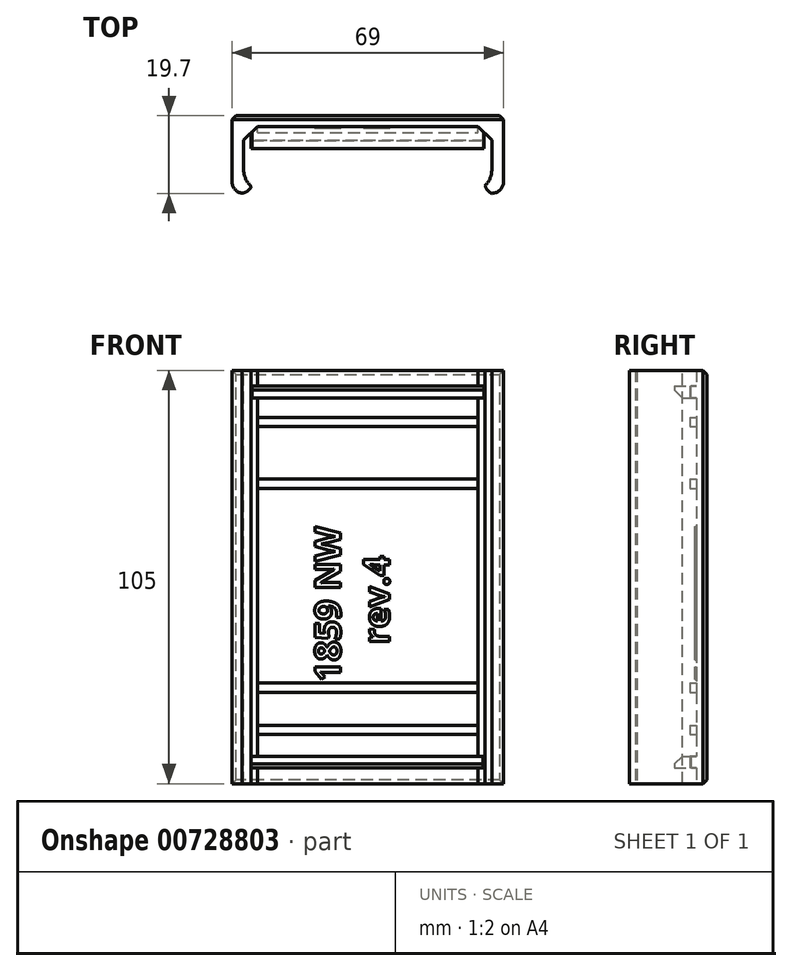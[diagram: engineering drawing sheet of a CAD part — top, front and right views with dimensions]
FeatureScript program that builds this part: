
annotation { "Feature Type Name" : "Feature", "Feature Type Description" : "" }
export const myFeature = defineFeature(function(context is Context, id is Id, definition is map)
    precondition{}
    {
        {
            var Q0;
            Q0=qCreatedBy(makeId("Top.planeOp"),FACE);
            var sketch = newSketch(context, id + "F0", { "sketchPlane" : qUnion([Q0])});
            skLineSegment(sketch, "E0", {"start": v(51.67, 0) * mm, "end": v(-17.33, 0) * mm});
            skLineSegment(sketch, "E1", {"start": v(-17.33, 0) * mm, "end": v(-17.33, -16.7) * mm});
            skLineSegment(sketch, "E2", {"start": v(-14.33, -19.7) * mm, "end": v(-12.53, -19.7) * mm});
            skLineSegment(sketch, "E3", {"start": v(-12.53, -19.7) * mm, "end": v(-12.53, -18.2) * mm});
            skLineSegment(sketch, "E4", {"start": v(-13.53, -17.2) * mm, "end": v(-14.33, -17.2) * mm});
            skLineSegment(sketch, "E5", {"start": v(-14.33, -17.2) * mm, "end": v(-14.33, -2.7) * mm});
            skLineSegment(sketch, "E6", {"start": v(-14.33, -2.7) * mm, "end": v(48.67, -2.7) * mm});
            skLineSegment(sketch, "E7", {"start": v(48.67, -2.7) * mm, "end": v(48.67, -17.2) * mm});
            skLineSegment(sketch, "E8", {"start": v(48.67, -17.2) * mm, "end": v(47.87, -17.2) * mm});
            skLineSegment(sketch, "E9", {"start": v(46.87, -18.2) * mm, "end": v(46.87, -19.7) * mm});
            skLineSegment(sketch, "E10", {"start": v(46.87, -19.7) * mm, "end": v(48.67, -19.7) * mm});
            skLineSegment(sketch, "E11", {"start": v(51.67, -16.7) * mm, "end": v(51.67, 0) * mm});
            skPoint(sketch, "E12.visualSharp", {"position": v(-17.33, 0) * mm});
            skLineSegment(sketch, "E12.filletArc", {"start": v(-17.33, 0) * mm, "end": v(-17.33, 0) * mm});
            skPoint(sketch, "E13.visualSharp", {"position": v(51.67, 0) * mm});
            skLineSegment(sketch, "E13.filletArc", {"start": v(51.67, 0) * mm, "end": v(51.67, 0) * mm});
            skLineSegment(sketch, "E14.filletArc", {"start": v(-14.33, -2.7) * mm, "end": v(-14.33, -2.7) * mm});
            skPoint(sketch, "E15.visualSharp", {"position": v(48.67, -2.7) * mm});
            skLineSegment(sketch, "E15.filletArc", {"start": v(48.67, -2.7) * mm, "end": v(48.67, -2.7) * mm});
            skPoint(sketch, "E16.visualSharp", {"position": v(-12.53, -17.2) * mm});
            skArc(sketch, "E16.filletArc", {"start": v(-12.53, -18.2) * mm, "mid": v(-12.82, -17.5) * mm, "end": v(-13.53, -17.2) * mm});
            skPoint(sketch, "E17.visualSharp", {"position": v(46.87, -17.2) * mm});
            skArc(sketch, "E17.filletArc", {"start": v(47.87, -17.2) * mm, "mid": v(47.17, -17.5) * mm, "end": v(46.87, -18.2) * mm});
            skPoint(sketch, "E18.visualSharp", {"position": v(51.67, -19.7) * mm});
            skArc(sketch, "E18.filletArc", {"start": v(48.67, -19.7) * mm, "mid": v(50.8, -18.82) * mm, "end": v(51.67, -16.7) * mm});
            skPoint(sketch, "E19.visualSharp", {"position": v(-17.33, -19.7) * mm});
            skArc(sketch, "E19.filletArc", {"start": v(-17.33, -16.7) * mm, "mid": v(-16.45, -18.82) * mm, "end": v(-14.33, -19.7) * mm});
            skLineSegment(sketch, "E20", {"start": v(17.17, 21.1) * mm, "end": v(17.17, -24.08) * mm, "construction": true});
            skPoint(sketch, "E20.startSnap0", {"position": v(17.17, 0) * mm});
            skSolve(sketch);
        }
        {
            var Q0;
            Q0=makeQuery(id+"F0.imprint","IMPRINT",FACE,{"disambiguationData":[TD([[makeQuery(id+"F0.imprint","IMPRINT",EDGE,{"derivedFrom":sQuery(id+"F0.wireOp",EDGE,"E0")}),1.0]])]});
            extrude(context, id + "F1", {"entities" : qUnion([Q0]), "depth" : 105 * mm, "offsetDistance" : 25 * mm});
        }
        {
            var Q0;
            Q0=makeQuery(id+"F1.opExtrude","SWEPT_EDGE",EDGE,{"disambiguationData":[OSD([sQuery(id+"F0.wireOp",EDGE,"E9"),sQuery(id+"F0.wireOp",EDGE,"E10")])]});
            var Q1;
            Q1=makeQuery(id+"F1.opExtrude","SWEPT_EDGE",EDGE,{"disambiguationData":[OSD([sQuery(id+"F0.wireOp",EDGE,"E2"),sQuery(id+"F0.wireOp",EDGE,"E3")])]});
            fillet(context, id + "F2", {"entities" : qUnion([Q0, Q1]), "radius" : 3 * mm, "tangentPropagation" : true, "allowEdgeOverflow" : false});
        }
        {
            var Q0;
            Q0=makeQuery(id+"F1.opExtrude","SWEPT_EDGE",EDGE,{"disambiguationData":[OSD([sQuery(id+"F0.wireOp",EDGE,"E7"),sQuery(id+"F0.wireOp",EDGE,"E8")])]});
            var Q1;
            Q1=makeQuery(id+"F1.opExtrude","SWEPT_EDGE",EDGE,{"disambiguationData":[OSD([sQuery(id+"F0.wireOp",EDGE,"E4"),sQuery(id+"F0.wireOp",EDGE,"E5")])]});
            fillet(context, id + "F3", {"entities" : qUnion([Q0, Q1]), "radius" : 5 * mm, "tangentPropagation" : true, "allowEdgeOverflow" : false});
        }
        {
            var Q0;
            Q0=makeQuery(id+"F1.opExtrude","SWEPT_FACE",FACE,{"disambiguationData":[OSD([sQuery(id+"F0.wireOp",EDGE,"E6")])]});
            var sketch = newSketch(context, id + "F4", { "sketchPlane" : qUnion([Q0])});
            skPoint(sketch, "E21", {"position": v(17.17, 52.5) * mm});
            skPoint(sketch, "E21.positionSnap0", {"position": v(48.67, 52.5) * mm});
            skPoint(sketch, "E21.positionSnap1", {"position": v(17.17, 105) * mm});
            skLineSegment(sketch, "E22.bottom", {"start": v(-9.33, 91) * mm, "end": v(43.67, 91) * mm});
            skLineSegment(sketch, "E22.top", {"start": v(-9.33, 14) * mm, "end": v(43.67, 14) * mm});
            skLineSegment(sketch, "E22.left", {"start": v(-9.33, 91) * mm, "end": v(-9.33, 14) * mm});
            skLineSegment(sketch, "E22.right", {"start": v(43.67, 91) * mm, "end": v(43.67, 14) * mm});
            skLineSegment(sketch, "E23.0", {"start": v(-6.33, 88) * mm, "end": v(40.67, 88) * mm});
            skLineSegment(sketch, "E23.1", {"start": v(-6.33, 88) * mm, "end": v(-6.33, 17) * mm});
            skLineSegment(sketch, "E23.2", {"start": v(-6.33, 17) * mm, "end": v(40.67, 17) * mm});
            skLineSegment(sketch, "E23.3", {"start": v(40.67, 88) * mm, "end": v(40.67, 17) * mm});
            skSolve(sketch);
        }
        {
            var Q0;
            Q0=makeQuery(id+"F2eu8U94Az3jvPq_1.boolean.opBoolean","SPLIT",FACE,{"disambiguationData":[TD([makeQuery(id+"F2eu8U94Az3jvPq_1.opExtrude","SWEPT_FACE",FACE,{"disambiguationData":[OSD([sQuery(id+"F4.wireOp",EDGE,"E23.0")])]})])],"derivedFrom":makeQuery(id+"F1.opExtrude","SWEPT_FACE",FACE,{"disambiguationData":[OSD([sQuery(id+"F0.wireOp",EDGE,"E6")])]})});
            var sketch = newSketch(context, id + "F5", { "sketchPlane" : qUnion([Q0])});
            skText(sketch, "E24", { "text": "1859 NW\n    rev.4", "fontName": "OpenSans-Bold.ttf"});
            const initialGuessF5  = {"E24": [0.01026, 0.02593, 0, 1, 0.00656]};
            skSetInitialGuess(sketch, initialGuessF5);
            skSolve(sketch);
        }
        {
            var Q0;
            Q0 = qSketchRegion(id + "F5", true);
            extrude(context, id + "F6", {"entities" : qUnion([Q0]), "operationType" : NewBodyOperationType.ADD, "depth" : .4 * mm, "offsetDistance" : 25 * mm});
        }
        {
            var Q0;
            Q0=makeQuery(id+"F1.opExtrude","SWEPT_EDGE",EDGE,{"disambiguationData":[OSD([sQuery(id+"F0.wireOp",EDGE,"E5"),sQuery(id+"F0.wireOp",EDGE,"E6")])]});
            var Q1;
            Q1=makeQuery(id+"F1.opExtrude","SWEPT_EDGE",EDGE,{"disambiguationData":[OSD([sQuery(id+"F0.wireOp",EDGE,"E6"),sQuery(id+"F0.wireOp",EDGE,"E7")])]});
            chamfer(context, id + "F7", {"entities" : qUnion([Q0, Q1]), "width" : 3.5 * mm, "tangentPropagation" : true});
        }
        {
            var Q0;
            Q0=makeQuery(id+"F1.opExtrude","SWEPT_EDGE",EDGE,{"disambiguationData":[OSD([sQuery(id+"F0.wireOp",EDGE,"E0"),sQuery(id+"F0.wireOp",EDGE,"E1")])]});
            var Q1;
            Q1=makeQuery(id+"F1.opExtrude","SWEPT_EDGE",EDGE,{"disambiguationData":[OSD([sQuery(id+"F0.wireOp",EDGE,"E0"),sQuery(id+"F0.wireOp",EDGE,"E11")])]});
            var Q2;
            Q2=makeQuery(id+"F1.opExtrude","CAP_EDGE",EDGE,{"disambiguationData":[OSD([sQuery(id+"F0.wireOp",EDGE,"E0")])],"isStart":false});
            var Q3;
            Q3=makeQuery(id+"F1.opExtrude","CAP_EDGE",EDGE,{"disambiguationData":[OSD([sQuery(id+"F0.wireOp",EDGE,"E0")])],"isStart":true});
            chamfer(context, id + "F8", {"entities" : qUnion([Q0, Q1, Q2, Q3]), "width" : 1 * mm, "tangentPropagation" : true});
        }
        {
            var Q0;
            {var subQ9=sQuery(id+"F0.wireOp",EDGE,"E6");var subQ10=sQuery(id+"F0.wireOp",EDGE,"E5");Q0=makeQuery(id+"F6.boolean.opBoolean","SPLIT",FACE,{"disambiguationData":[TD([makeQuery(id+"F1.opExtrude","SWEPT_FACE",FACE,{"disambiguationData":[OSD([subQ10])]})])],"derivedFrom":makeQuery(id+"F1.opExtrude","SWEPT_FACE",FACE,{"disambiguationData":[OSD([subQ9])]})});}
            var sketch = newSketch(context, id + "F9", { "sketchPlane" : qUnion([Q0])});
            skLineSegment(sketch, "E25.bottom", {"start": v(-10.83, 93.1) * mm, "end": v(45.17, 93.1) * mm});
            skLineSegment(sketch, "E25.top", {"start": v(-10.83, 90.75) * mm, "end": v(45.17, 90.75) * mm});
            skLineSegment(sketch, "E25.left", {"start": v(-10.83, 93.1) * mm, "end": v(-10.83, 90.75) * mm});
            skLineSegment(sketch, "E25.right", {"start": v(45.17, 93.1) * mm, "end": v(45.17, 90.75) * mm});
            skLineSegment(sketch, "E26.bottom", {"start": v(-10.83, 77.4) * mm, "end": v(45.17, 77.4) * mm});
            skLineSegment(sketch, "E26.top", {"start": v(-10.83, 75.05) * mm, "end": v(45.17, 75.05) * mm});
            skLineSegment(sketch, "E26.left", {"start": v(-10.83, 77.4) * mm, "end": v(-10.83, 75.05) * mm});
            skLineSegment(sketch, "E26.right", {"start": v(45.17, 77.4) * mm, "end": v(45.17, 75.05) * mm});
            skLineSegment(sketch, "E27.bottom", {"start": v(-10.83, 25.58) * mm, "end": v(45.17, 25.58) * mm});
            skLineSegment(sketch, "E27.top", {"start": v(-10.83, 23.23) * mm, "end": v(45.17, 23.23) * mm});
            skLineSegment(sketch, "E27.left", {"start": v(-10.83, 25.58) * mm, "end": v(-10.83, 23.23) * mm});
            skLineSegment(sketch, "E27.right", {"start": v(45.17, 25.58) * mm, "end": v(45.17, 23.23) * mm});
            skLineSegment(sketch, "E28.bottom", {"start": v(-10.83, 14.86) * mm, "end": v(45.17, 14.86) * mm});
            skLineSegment(sketch, "E28.top", {"start": v(-10.83, 12.52) * mm, "end": v(45.17, 12.52) * mm});
            skLineSegment(sketch, "E28.left", {"start": v(-10.83, 14.86) * mm, "end": v(-10.83, 12.52) * mm});
            skLineSegment(sketch, "E28.right", {"start": v(45.17, 14.86) * mm, "end": v(45.17, 12.52) * mm});
            skLineSegment(sketch, "E29.bottom", {"start": v(-12.26, 101) * mm, "end": v(46.74, 101) * mm});
            skLineSegment(sketch, "E29.top", {"start": v(-12.26, 98) * mm, "end": v(46.74, 98) * mm});
            skLineSegment(sketch, "E29.left", {"start": v(-12.26, 101) * mm, "end": v(-12.26, 98) * mm});
            skLineSegment(sketch, "E29.right", {"start": v(46.74, 101) * mm, "end": v(46.74, 98) * mm});
            skLineSegment(sketch, "E30.bottom", {"start": v(-12.5, 7) * mm, "end": v(46.5, 7) * mm});
            skLineSegment(sketch, "E30.top", {"start": v(-12.5, 4) * mm, "end": v(46.5, 4) * mm});
            skLineSegment(sketch, "E30.left", {"start": v(-12.5, 7) * mm, "end": v(-12.5, 4) * mm});
            skLineSegment(sketch, "E30.right", {"start": v(46.5, 7) * mm, "end": v(46.5, 4) * mm});
            skSolve(sketch);
        }
        {
            var Q0;
            Q0 = qSketchRegion(id + "F9", true);
            extrude(context, id + "F10", {"entities" : qUnion([Q0]), "operationType" : NewBodyOperationType.ADD, "depth" : 1.6 * mm, "offsetDistance" : 25 * mm});
        }
        {
            var Q0;
            Q0=makeQuery(id+"F10.opExtrude","CAP_FACE",FACE,{"disambiguationData":[OSD([sQuery(id+"F9.wireOp",EDGE,"E30.bottom"),sQuery(id+"F9.wireOp",EDGE,"E30.top"),sQuery(id+"F9.wireOp",EDGE,"E30.left"),sQuery(id+"F9.wireOp",EDGE,"E30.right")])],"isStart":false});
            var Q1;
            Q1=makeQuery(id+"F10.opExtrude","CAP_FACE",FACE,{"disambiguationData":[OSD([sQuery(id+"F9.wireOp",EDGE,"E29.bottom"),sQuery(id+"F9.wireOp",EDGE,"E29.top"),sQuery(id+"F9.wireOp",EDGE,"E29.left"),sQuery(id+"F9.wireOp",EDGE,"E29.right")])],"isStart":false});
            extrude(context, id + "F11", {"entities" : qUnion([Q0, Q1]), "operationType" : NewBodyOperationType.ADD, "depth" : 4 * mm, "offsetDistance" : 25 * mm});
        }
        {
            var Q0;
            Q0=makeQuery(id+"F11.opExtrude","CAP_EDGE",EDGE,{"disambiguationData":[OSD([sQuery(id+"F9.wireOp",EDGE,"E29.top")])],"isStart":false});
            var Q1;
            Q1=makeQuery(id+"F11.opExtrude","CAP_EDGE",EDGE,{"disambiguationData":[OSD([sQuery(id+"F9.wireOp",EDGE,"E30.bottom")])],"isStart":false});
            chamfer(context, id + "F12", {"entities" : qUnion([Q0, Q1]), "width" : 2 * mm, "tangentPropagation" : true});
        }
    });
